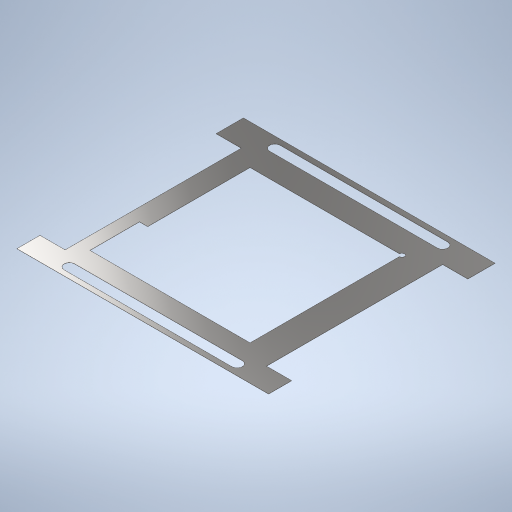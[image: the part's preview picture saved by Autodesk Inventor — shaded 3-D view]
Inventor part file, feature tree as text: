
AUTODESK INVENTOR PART (.ipt)
format: ipt  version: 2023 (Build 270158000, 158)  size: 325,632 bytes
history: native  units: in
note: dims shown in document units (in); Inventor stores cm internally (conversion verified against a paired STEP export)
features: extrude x5, sketch x5
ambient origin geometry x8: Origin, YZ Plane, XZ Plane, XY Plane, X Axis, Y Axis, Z Axis, Center Point
bodies: Solid1 (feature_tree)
feature tree (10):
  extrude  "Extrusion1"  Depth=2.7in
  extrude  "Extrusion2"  TaperAngle=0.0deg  [1 undecoded]
  extrude  "Extrusion3"  Depth=0.3in
  extrude  "Extrusion4"  Depth=0.125in
  extrude  "Extrusion5"  Depth=0.0984in
  sketch  "Sketch1"  dims[d0=3.0in d1=2.7in]
  sketch  "Sketch2"  dims[d2=0.002in d3=0.0in d7=0.0in d8=0.0in]
  sketch  "Sketch3"  dims[d13=2.1in d14=0.3in]
  sketch  "Sketch4"  dims[d16=0.325in d17=0.125in]
  sketch  "Sketch5"  dims[d18=0.125in d19=2.0in d20=2.0in d21=0.125in d22=0.125in d23=1.0in d24=0.0in d27=0.0in d28=0.0in d29=0.0625in d30=2.35in d31=1.8in d32=0.313in d33=0.0217in d34=1.811in d35=1.811in d36=0.5906in d37=0.0984in d38=0.0in d39=0.0in]
note: 1 required parameter value undecoded (feature->parameter linkage not recoverable at this tier; creation-order binding heuristic only, values carry confidence <= 0.55)
